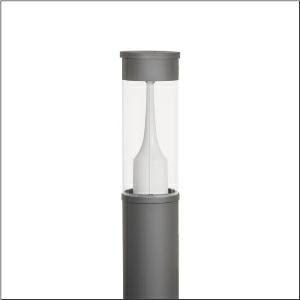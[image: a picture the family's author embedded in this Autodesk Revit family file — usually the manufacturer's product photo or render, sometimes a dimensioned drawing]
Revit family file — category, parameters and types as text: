
# Revit family: city-light_260_iq___p1_0a_5xa5295nf14h_1e18
name_source: partatom
category: Lighting Fixtures
units: mm (PartAtom-declared; Revit-internal decimal feet)

## family parameters
Cut with Voids When Loaded = No
Host = Face
Light Source = No
Part Type = Normal
Room Calculation Point = No
Round Connector Dimension = Use Diameter
Shared = No

## types (1)
- --- (1 x LED, 1510 lm, 11.8 W, 2700K)
    Apparent Load = 12 VA
    CIE Flux Codes = 32 61 90 93 100
    Color Rendering = 70
    Color Temperature = 2700K
    Default Elevation = 1800 mm
    Description = City-Light 260 iQ, light pillar, Module 540 iQ-SR, primary light control with 3 zone facetted reflector, of plastic, silver coated, highly specular, structured, primary optical cover: cover, of PMMA, transparent, partly coated, light distribution: P1.0a, primary light characteristic: strongly asymmetric, LED, High Power LED, rated luminous flux: 1.510lm, luminous efficacy: 128lm/W, light colour: 727, colour temperature: 2700K, control gear: ECG iQ, control: presetting dimming logarithmic, Street-Remote, Auto-Match, Temp-Guard, Lumen-Switch, Night-Set, Smart-Wire, Light-Fading, Desk-Remote (wireless, voltage-free reading and setting of iQ features in the workshop via application-optimized NFC function/RFID function), optimised constant luminous flux control (CLO 2.0), with terminal, 6-pole, max. 2.5mm², mains connection: 230..240V, AC, 50/60Hz, start of lifetime: 12W, end of service life: 12W, reduction: 6W, luminaire housing, cylindrical, of extruded aluminium section, coated, Siteco® metallic grey (DB 702S), length: 2.600mm, diameter: 200mm, Module 540 iQ-SR, traffic white (RAL 9016), equipment: standard, protection rating (complete): IP65, insulation class (complete): insulation class II (safety insulation), certification: CE, ENEC, VDE, packaging unit: 1 piece

Light Distribution: P1.0a
    Height = 500 mm
    Lamp = 1 x LED
    Lamp Light Flux = 1510 lm
    Lamp Power = 11.8 W
    Lamp count = 1
    Length = 200 mm  [stored 0.656168 ft]
    Luminous efficacy = 128 lm/W
    Manufacturer = Siteco
    ModVariant = No
    Model = 5XA5295NF14H
    Mounting Place = Floor
    Mounting Type = Freestanding
    Number of Poles = 1
    OnlyDefault = Yes
    Power Factor = 1
    Product Name = City-Light 260 iQ | P1.0a
    Product group = light pillar
    ProductGroupID = 1303
    Protection Class = Protection class II
    Protection Degree = IP 65
    RLX_Detail_Level = 1
    RLX_Emergency_Light_Flux = 0 lm
    RLX_Emergency_Type = 0
    RLX_Emergency_Type_DB = No
    RlxData = <blob elided: 52549 chars, md5=42083fdf>
    Socket = socket
    Standby Power = 0 W
    System Light Flux = 1510 lm
    System Power = 12 W
    Type Comments = factory setting: luminous flux: 100 % | dim-lin: 254 | 472 mA
    Type Image = l_1006918.jpg
    URL = http://relux.com
    VarID = @adj_085455
    Voltage = 0 V
    Weight = 0.00 kg
    Width = 0 mm  [stored 0 ft]

note: [stored X ft] marks values corroborated as IEEE doubles in the binary element streams (Revit-internal decimal feet)

## geometry (parser evidence)
native form markers: Blend x4, Sweep x12
no freeform markers — native parametric forms only
